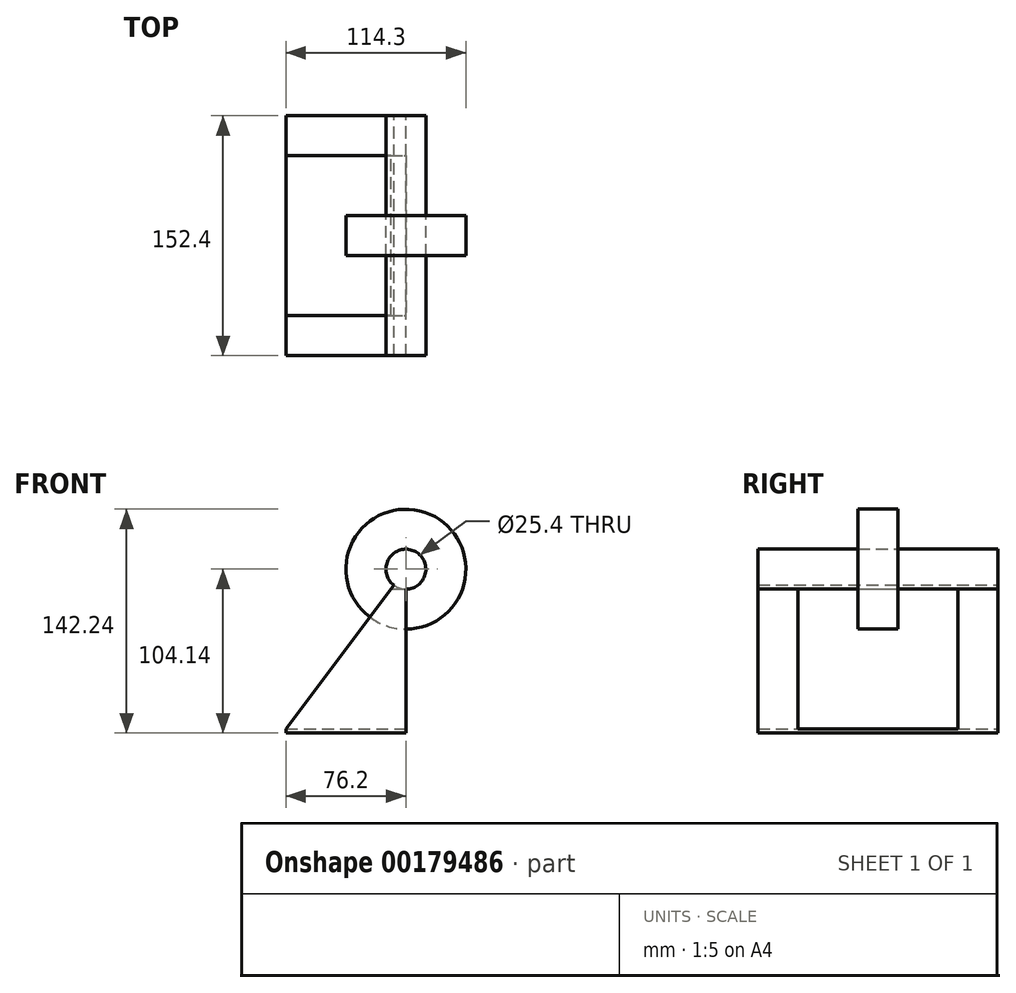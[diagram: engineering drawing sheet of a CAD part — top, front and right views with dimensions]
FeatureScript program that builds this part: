
annotation { "Feature Type Name" : "Feature", "Feature Type Description" : "" }
export const myFeature = defineFeature(function(context is Context, id is Id, definition is map)
    precondition{}
    {
        {
            var Q0;
            Q0=qCreatedBy(makeId("Front.planeOp"),FACE);
            var sketch = newSketch(context, id + "F0", { "sketchPlane" : qUnion([Q0])});
            skLineSegment(sketch, "E0", {"start": v(0, 0) * mm, "end": v(-76.2, -101.6) * mm});
            skLineSegment(sketch, "E1", {"start": v(-76.2, -101.6) * mm, "end": v(0, -101.6) * mm});
            skLineSegment(sketch, "E2", {"start": v(0, -101.6) * mm, "end": v(0, 0) * mm});
            skCircle(sketch, "E3", {"center": v(0, 0) * mm, "radius": 38.1 * mm});
            skCircle(sketch, "E4", {"center": v(0, 0) * mm, "radius": 12.7 * mm});
            skLineSegment(sketch, "E5.top", {"start": v(-76.2, -104.14) * mm, "end": v(0, -104.14) * mm});
            skLineSegment(sketch, "E5.left", {"start": v(-76.2, -101.6) * mm, "end": v(-76.2, -104.14) * mm});
            skLineSegment(sketch, "E5.right", {"start": v(0, -101.6) * mm, "end": v(0, -104.14) * mm});
            skSolve(sketch);
        }
        {
            var Q0;
            Q0=makeQuery(id+"F0.imprint","IMPRINT",FACE,{"disambiguationData":[TD([[makeQuery(id+"F0.imprint","IMPRINT",EDGE,{"derivedFrom":sQuery(id+"F0.wireOp",EDGE,"E1")}),-1.0]])]});
            extrude(context, id + "F1", {"entities" : qUnion([Q0]), "endBound" : BoundingType.SYMMETRIC, "depth" : 152.4 * mm});
        }
        {
            var Q0;
            {var subQ0=sQuery(id+"F0.wireOp",EDGE,"E1");Q0=makeQuery(id+"F0.imprint","IMPRINT",FACE,{"disambiguationData":[TD([[makeQuery(id+"F0.imprint","IMPRINT",EDGE,{"derivedFrom":subQ0}),1.0]])]});}
            var Q1;
            {var subQ0=sQuery(id+"F0.wireOp",EDGE,"E2");var subQ1=sQuery(id+"F0.wireOp",EDGE,"E0");var subQ2=makeQuery(id+"F0.imprint","INTERSECT",VERTEX,{"derivedFrom":[subQ1,subQ0]});Q1=makeQuery(id+"F0.imprint","IMPRINT",FACE,{"disambiguationData":[TD([[makeQuery(id+"F0.imprint","IMPRINT",EDGE,{"disambiguationData":[TD([[subQ2,-1.0]])],"derivedFrom":subQ1}),-1.0]])]});}
            var Q2;
            {var subQ0=sQuery(id+"F0.wireOp",EDGE,"E3");var subQ1=sQuery(id+"F0.wireOp",EDGE,"E0");var subQ2=makeQuery(id+"F0.imprint","INTERSECT",VERTEX,{"derivedFrom":[subQ1,subQ0]});Q2=makeQuery(id+"F0.imprint","IMPRINT",FACE,{"disambiguationData":[TD([[makeQuery(id+"F0.imprint","IMPRINT",EDGE,{"disambiguationData":[TD([[subQ2,1.0]])],"derivedFrom":subQ1}),1.0]])]});}
            var Q3;
            {var subQ0=sQuery(id+"F0.wireOp",EDGE,"E2");var subQ1=sQuery(id+"F0.wireOp",EDGE,"E0");var subQ2=makeQuery(id+"F0.imprint","INTERSECT",VERTEX,{"derivedFrom":[subQ1,subQ0]});Q3=makeQuery(id+"F0.imprint","IMPRINT",FACE,{"disambiguationData":[TD([[makeQuery(id+"F0.imprint","IMPRINT",EDGE,{"disambiguationData":[TD([[subQ2,-1.0]])],"derivedFrom":subQ1}),1.0]])]});}
            extrude(context, id + "F2", {"entities" : qUnion([Q0, Q1, Q2, Q3]), "operationType" : NewBodyOperationType.ADD, "endBound" : BoundingType.SYMMETRIC, "depth" : 152.4 * mm});
        }
        {
            var Q0;
            Q0=makeQuery(id+"F2.boolean.opBoolean","MERGE",FACE,{"derivedFrom":[makeQuery(id+"F1.opExtrude","SWEPT_FACE",FACE,{"disambiguationData":[OSD([sQuery(id+"F0.wireOp",EDGE,"E5.right")])]}),makeQuery(id+"F2.opExtrude","SWEPT_FACE",FACE,{"disambiguationData":[OSD([sQuery(id+"F0.wireOp",EDGE,"E2")])]})]});
            var sketch = newSketch(context, id + "F3", { "sketchPlane" : qUnion([Q0])});
            skLineSegment(sketch, "E6.bottom", {"start": v(50.8, -12.7) * mm, "end": v(-50.8, -12.7) * mm});
            skLineSegment(sketch, "E6.top", {"start": v(50.8, -101.6) * mm, "end": v(-50.8, -101.6) * mm});
            skLineSegment(sketch, "E6.left", {"start": v(50.8, -12.7) * mm, "end": v(50.8, -101.6) * mm});
            skLineSegment(sketch, "E6.right", {"start": v(-50.8, -12.7) * mm, "end": v(-50.8, -101.6) * mm});
            skPoint(sketch, "E6.middle", {"position": v(0, -57.15) * mm});
            skSolve(sketch);
        }
        {
            var Q0;
            Q0=makeQuery(id+"F3.imprint","IMPRINT",FACE,{"disambiguationData":[TD([[makeQuery(id+"F3.imprint","IMPRINT",EDGE,{"derivedFrom":sQuery(id+"F3.wireOp",EDGE,"E6.bottom")}),-1.0]])]});
            extrude(context, id + "F4", {"entities" : qUnion([Q0]), "operationType" : NewBodyOperationType.REMOVE, "endBound" : BoundingType.THROUGH_ALL, "oppositeDirection" : true, "depth" : 25.4 * mm});
        }
        {
            var Q0;
            {var subQ0=sQuery(id+"F0.wireOp",EDGE,"E3");var subQ1=sQuery(id+"F0.wireOp",EDGE,"E0");var subQ2=makeQuery(id+"F0.imprint","INTERSECT",VERTEX,{"derivedFrom":[subQ1,subQ0]});Q0=makeQuery(id+"F0.imprint","IMPRINT",FACE,{"disambiguationData":[TD([[makeQuery(id+"F0.imprint","IMPRINT",EDGE,{"disambiguationData":[TD([[subQ2,1.0]])],"derivedFrom":subQ1}),-1.0]])]});}
            var Q1;
            {var subQ0=sQuery(id+"F0.wireOp",EDGE,"E3");var subQ1=sQuery(id+"F0.wireOp",EDGE,"E0");var subQ2=makeQuery(id+"F0.imprint","INTERSECT",VERTEX,{"derivedFrom":[subQ1,subQ0]});Q1=makeQuery(id+"F0.imprint","IMPRINT",FACE,{"disambiguationData":[TD([[makeQuery(id+"F0.imprint","IMPRINT",EDGE,{"disambiguationData":[TD([[subQ2,1.0]])],"derivedFrom":subQ1}),1.0]])]});}
            extrude(context, id + "F5", {"entities" : qUnion([Q0, Q1]), "endBound" : BoundingType.SYMMETRIC, "depth" : 25.4 * mm});
        }
    });
